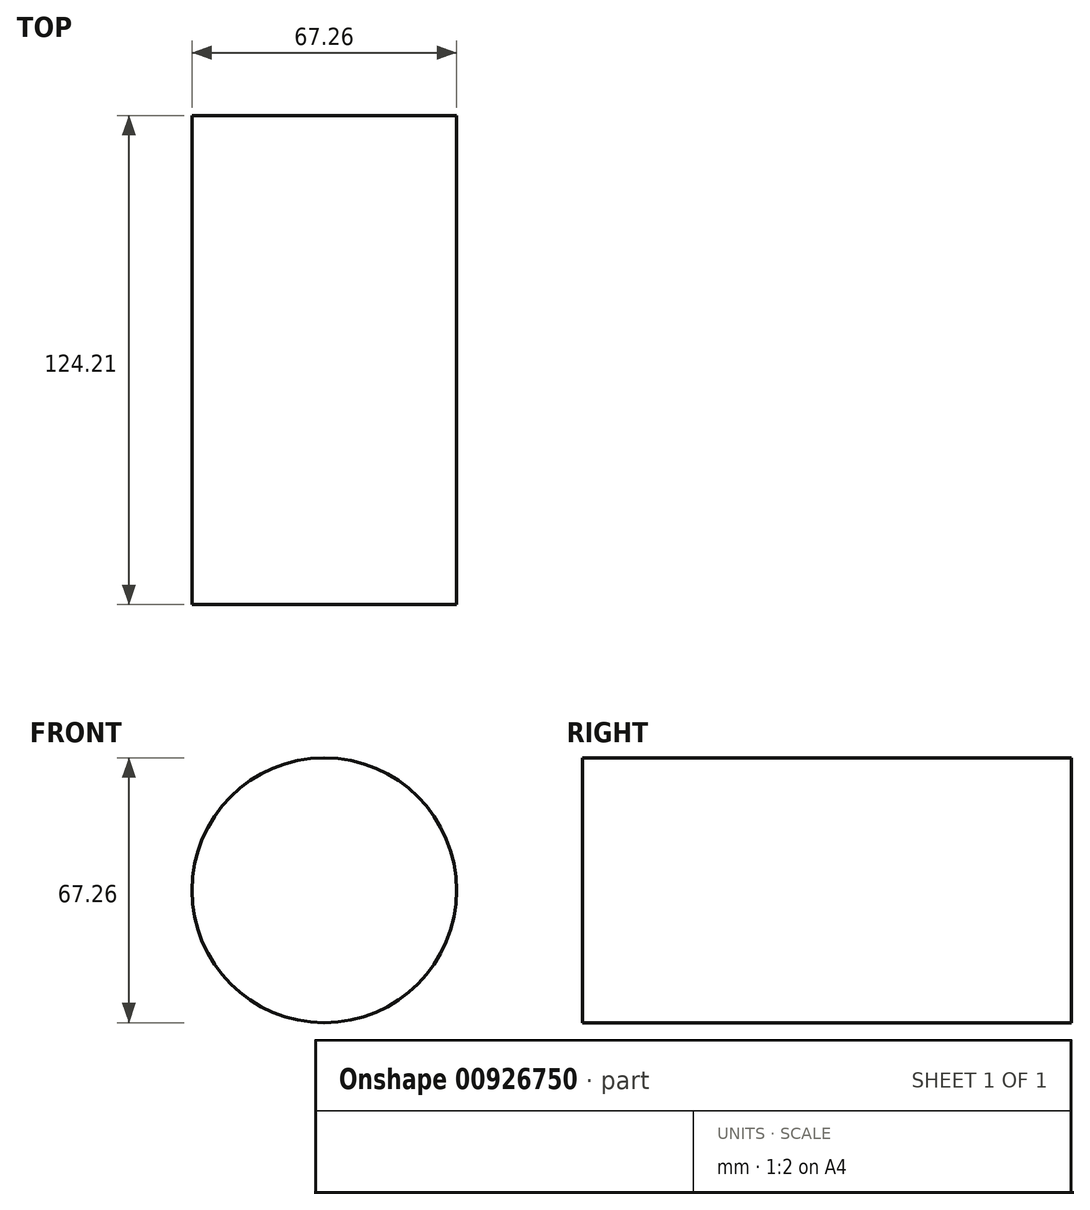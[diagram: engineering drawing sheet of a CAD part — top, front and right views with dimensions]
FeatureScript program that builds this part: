
annotation { "Feature Type Name" : "Feature", "Feature Type Description" : "" }
export const myFeature = defineFeature(function(context is Context, id is Id, definition is map)
    precondition{}
    {
        {
            var Q0;
            Q0=qCreatedBy(makeId("Front.planeOp"),FACE);
            var sketch = newSketch(context, id + "F0", { "sketchPlane" : qUnion([Q0])});
            skCircle(sketch, "E0", {"center": v(0, 0) * mm, "radius": 33.63 * mm});
            skSolve(sketch);
        }
        {
            var Q0;
            Q0 = qSketchRegion(id + "F0", true);
            extrude(context, id + "F1", {"entities" : qUnion([Q0]), "depth" : 124.2 * mm, "offsetDistance" : 25.4 * mm});
        }
    });
